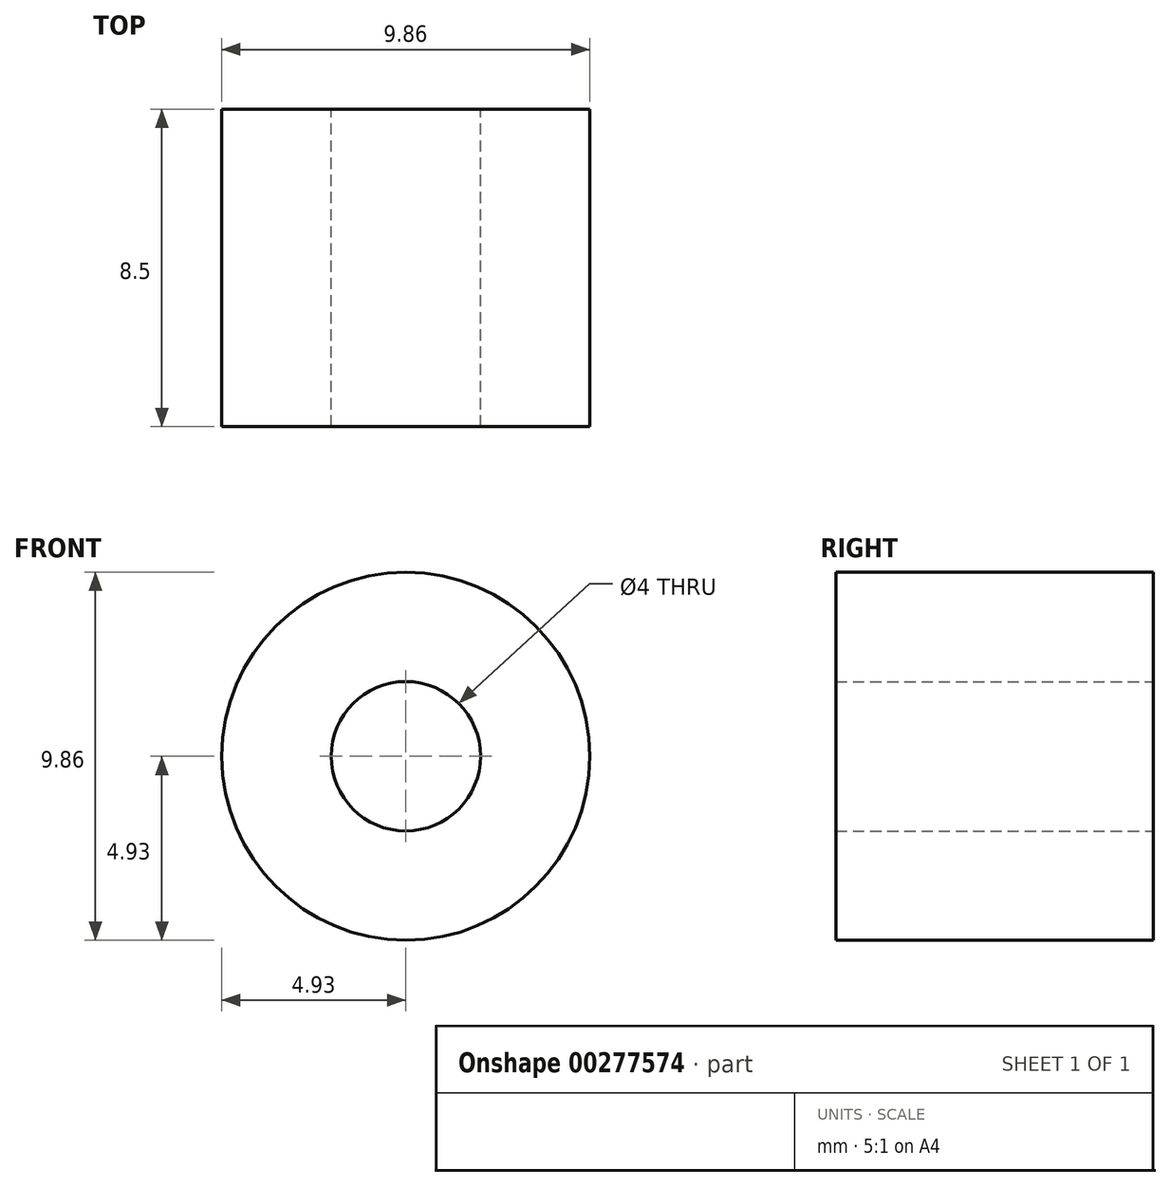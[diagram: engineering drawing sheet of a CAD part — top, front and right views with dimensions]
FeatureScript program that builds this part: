
annotation { "Feature Type Name" : "Feature", "Feature Type Description" : "" }
export const myFeature = defineFeature(function(context is Context, id is Id, definition is map)
    precondition{}
    {
        {
            var Q0;
            Q0=qCreatedBy(makeId("Front.planeOp"),FACE);
            var sketch = newSketch(context, id + "F0", { "sketchPlane" : qUnion([Q0])});
            skCircle(sketch, "E0", {"center": v(0, 0) * mm, "radius": 4.92 * mm});
            skCircle(sketch, "E1", {"center": v(0, 0) * mm, "radius": 2 * mm});
            skSolve(sketch);
        }
        {
            var Q0;
            Q0=makeQuery(id+"F0.imprint","IMPRINT",FACE,{"disambiguationData":[TD([[makeQuery(id+"F0.imprint","IMPRINT",EDGE,{"derivedFrom":sQuery(id+"F0.wireOp",EDGE,"E0")}),1.0]])]});
            extrude(context, id + "F1", {"entities" : qUnion([Q0]), "depth" : 8.5 * mm, "offsetDistance" : 25 * mm});
        }
    });
